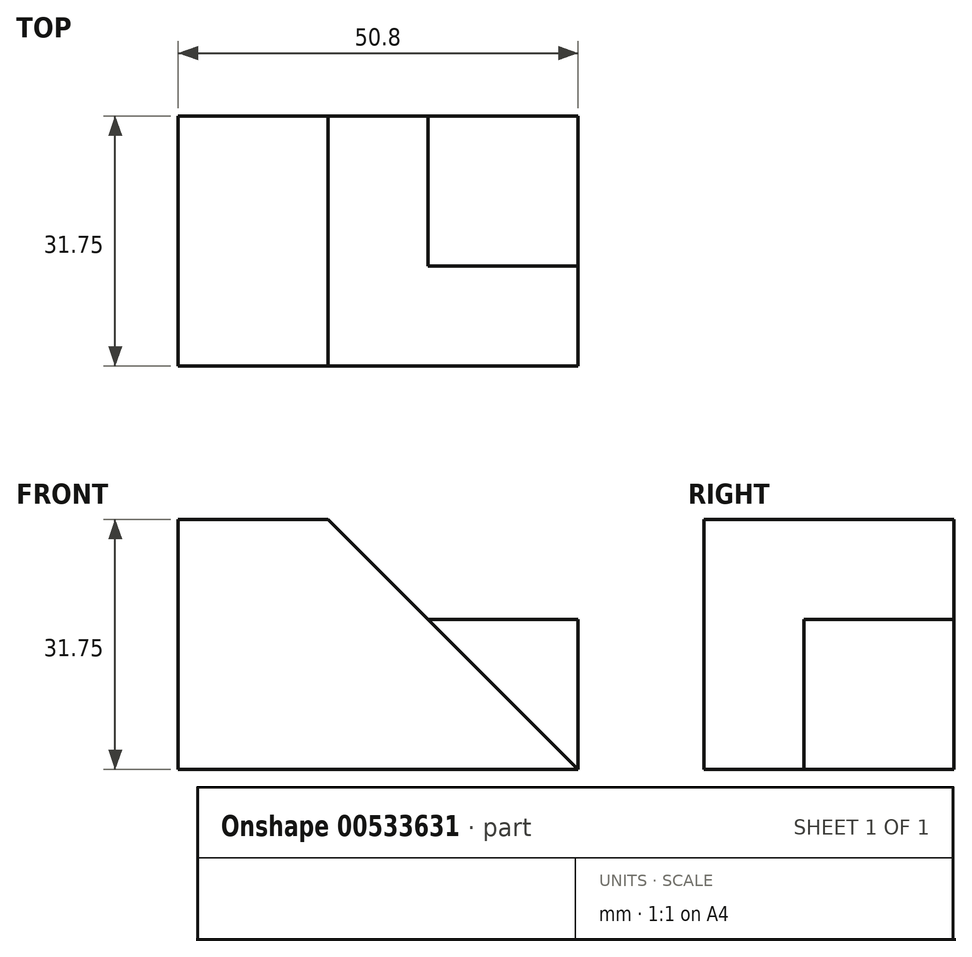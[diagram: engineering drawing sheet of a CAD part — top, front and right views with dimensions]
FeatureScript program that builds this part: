
annotation { "Feature Type Name" : "Feature", "Feature Type Description" : "" }
export const myFeature = defineFeature(function(context is Context, id is Id, definition is map)
    precondition{}
    {
        {
            var Q0;
            Q0=qCreatedBy(makeId("Front.planeOp"),FACE);
            var sketch = newSketch(context, id + "F0", { "sketchPlane" : qUnion([Q0])});
            skLineSegment(sketch, "E0", {"start": v(-92.1, 0) * mm, "end": v(-92.1, 31.75) * mm});
            skLineSegment(sketch, "E1", {"start": v(-92.1, 31.75) * mm, "end": v(-41.3, 31.75) * mm});
            skLineSegment(sketch, "E2", {"start": v(-41.3, 31.75) * mm, "end": v(-41.3, 0) * mm});
            skLineSegment(sketch, "E3", {"start": v(-41.3, 0) * mm, "end": v(-92.1, 0) * mm});
            skSolve(sketch);
        }
        {
            var Q0;
            Q0=makeQuery(id+"F0.imprint","IMPRINT",FACE,{"disambiguationData":[TD([[makeQuery(id+"F0.imprint","IMPRINT",EDGE,{"derivedFrom":sQuery(id+"F0.wireOp",EDGE,"E0")}),-1.0]])]});
            extrude(context, id + "F1", {"entities" : qUnion([Q0]), "depth" : 31.75 * mm, "offsetDistance" : 25.4 * mm});
        }
        {
            var Q0;
            Q0=makeQuery(id+"F1.opExtrude","CAP_FACE",FACE,{"disambiguationData":[OSD([sQuery(id+"F0.wireOp",EDGE,"E0"),sQuery(id+"F0.wireOp",EDGE,"E1"),sQuery(id+"F0.wireOp",EDGE,"E2"),sQuery(id+"F0.wireOp",EDGE,"E3")])],"isStart":false});
            var sketch = newSketch(context, id + "F2", { "sketchPlane" : qUnion([Q0])});
            skLineSegment(sketch, "E4", {"start": v(-73.05, 31.75) * mm, "end": v(-41.3, 0) * mm});
            skSolve(sketch);
        }
        {
            var Q0;
            {var subQ0=sQuery(id+"F2.wireOp",EDGE,"E4");Q0=makeQuery(id+"F2.imprint","IMPRINT",FACE,{"disambiguationData":[TD([[makeQuery(id+"F2.imprint","IMPRINT",EDGE,{"derivedFrom":subQ0}),1.0]])]});}
            extrude(context, id + "F3", {"entities" : qUnion([Q0]), "operationType" : NewBodyOperationType.REMOVE, "oppositeDirection" : true, "depth" : 12.7 * mm, "offsetDistance" : 25.4 * mm});
        }
        {
            var Q0;
            Q0=makeQuery(id+"F3.boolean.opBoolean","COPY",FACE,{"derivedFrom":makeQuery(id+"F3.opExtrude","CAP_FACE",FACE,{"disambiguationData":[OSD([sQuery(id+"F0.wireOp",EDGE,"E1"),sQuery(id+"F0.wireOp",EDGE,"E2"),sQuery(id+"F2.wireOp",EDGE,"E4")])],"isStart":false})});
            var sketch = newSketch(context, id + "F4", { "sketchPlane" : qUnion([Q0])});
            skLineSegment(sketch, "E5", {"start": v(-41.3, 0) * mm, "end": v(-73.05, 31.75) * mm});
            skSolve(sketch);
        }
        {
            var Q0;
            Q0=makeQuery(id+"F4.imprint","IMPRINT",FACE,{"disambiguationData":[TD([[makeQuery(id+"F4.imprint","IMPRINT",EDGE,{"derivedFrom":sQuery(id+"F4.wireOp",EDGE,"E5")}),1.0]])]});
            extrude(context, id + "F5", {"entities" : qUnion([Q0]), "operationType" : NewBodyOperationType.REMOVE, "endBound" : BoundingType.THROUGH_ALL, "oppositeDirection" : true, "depth" : 25.4 * mm, "offsetDistance" : 25.4 * mm});
        }
        {
            var Q0;
            Q0=qCreatedBy(makeId("Front.planeOp"),FACE);
            var sketch = newSketch(context, id + "F6", { "sketchPlane" : qUnion([Q0])});
            skLineSegment(sketch, "E6", {"start": v(-41.3, 0) * mm, "end": v(-41.3, 19.05) * mm});
            skLineSegment(sketch, "E7", {"start": v(-41.3, 19.05) * mm, "end": v(-60.35, 19.05) * mm});
            skLineSegment(sketch, "E8", {"start": v(-60.35, 19.05) * mm, "end": v(-60.35, 0) * mm});
            skLineSegment(sketch, "E9", {"start": v(-60.35, 0) * mm, "end": v(-41.3, 0) * mm});
            skSolve(sketch);
        }
        {
            var Q0;
            Q0=makeQuery(id+"F6.imprint","IMPRINT",FACE,{"disambiguationData":[TD([[makeQuery(id+"F6.imprint","IMPRINT",EDGE,{"derivedFrom":sQuery(id+"F6.wireOp",EDGE,"E6")}),1.0]])]});
            extrude(context, id + "F7", {"entities" : qUnion([Q0]), "operationType" : NewBodyOperationType.ADD, "depth" : 19.05 * mm, "offsetDistance" : 25.4 * mm});
        }
    });
